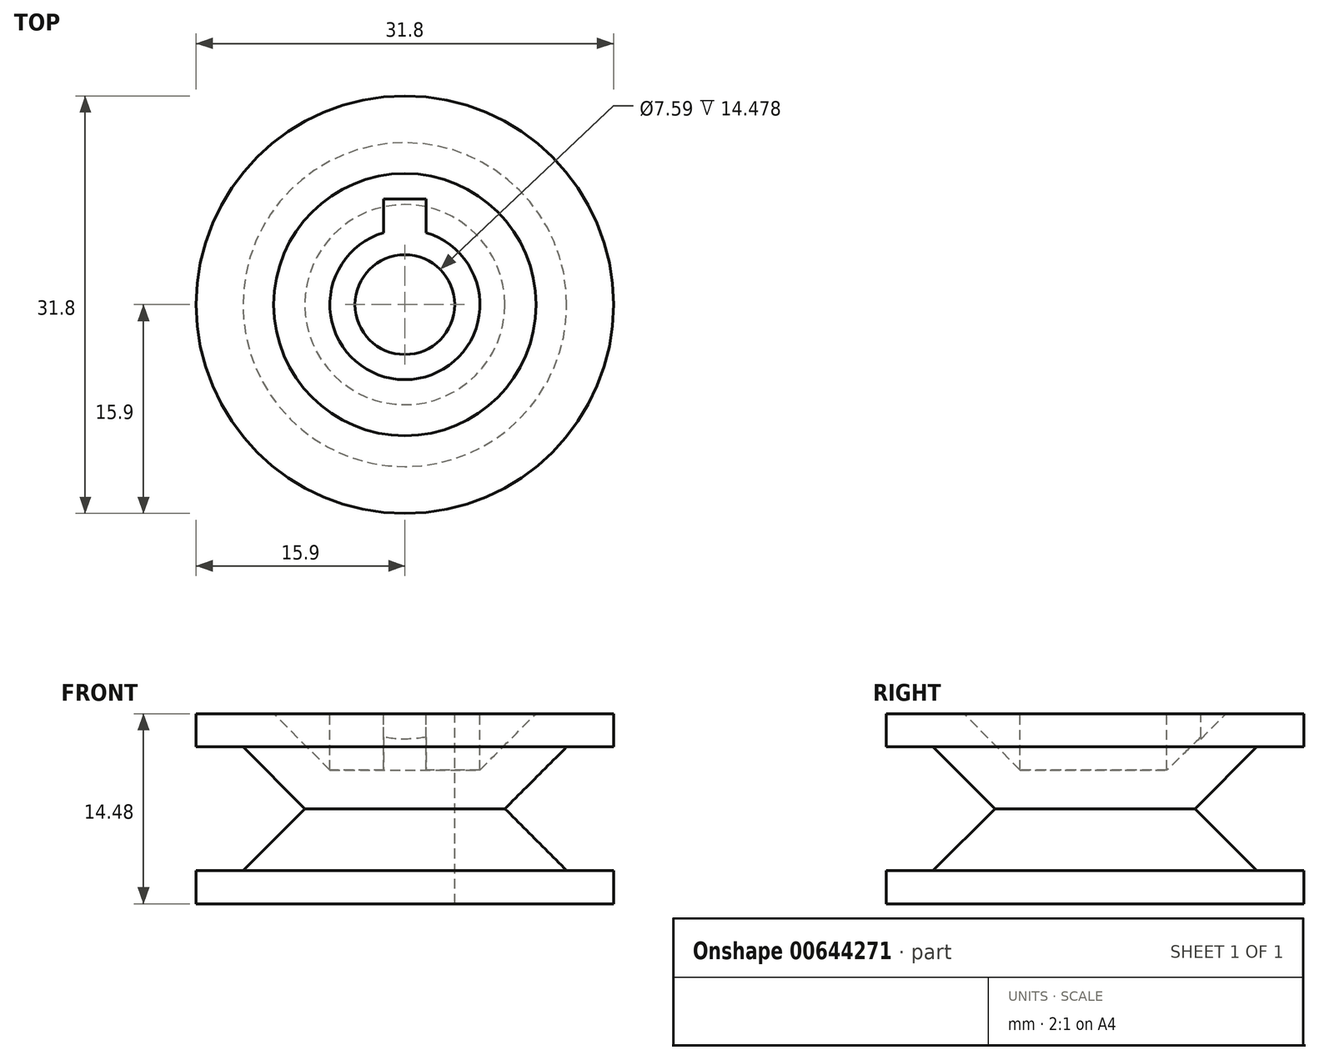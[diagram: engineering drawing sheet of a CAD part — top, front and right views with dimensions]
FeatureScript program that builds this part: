
annotation { "Feature Type Name" : "Feature", "Feature Type Description" : "" }
export const myFeature = defineFeature(function(context is Context, id is Id, definition is map)
    precondition{}
    {
        {
            var Q0;
            Q0=qCreatedBy(makeId("Top.planeOp"),FACE);
            var sketch = newSketch(context, id + "F0", { "sketchPlane" : qUnion([Q0])});
            skCircle(sketch, "E0", {"center": v(0, 0) * mm, "radius": 15.9 * mm});
            skSolve(sketch);
        }
        {
            var Q0;
            Q0 = qSketchRegion(id + "F0", true);
            extrude(context, id + "F1", {"entities" : qUnion([Q0]), "endBound" : BoundingType.SYMMETRIC, "depth" : 14.48 * mm, "offsetDistance" : 25.4 * mm});
        }
        {
            var Q0;
            Q0=makeQuery(id+"F1.opExtrude","CAP_FACE",FACE,{"disambiguationData":[OSD([sQuery(id+"F0.wireOp",EDGE,"E0")])],"isStart":false});
            var sketch = newSketch(context, id + "F2", { "sketchPlane" : qUnion([Q0])});
            skCircle(sketch, "E1", {"center": v(0, 0) * mm, "radius": 3.8 * mm});
            skSolve(sketch);
        }
        {
            var Q0;
            Q0=makeQuery(id+"F2.imprint","IMPRINT",FACE,{"disambiguationData":[TD([[makeQuery(id+"F2.imprint","IMPRINT",EDGE,{"derivedFrom":sQuery(id+"F2.wireOp",EDGE,"E1")}),1.0]])]});
            extrude(context, id + "F3", {"entities" : qUnion([Q0]), "operationType" : NewBodyOperationType.REMOVE, "endBound" : BoundingType.THROUGH_ALL, "oppositeDirection" : true, "depth" : 25.4 * mm, "offsetDistance" : 25.4 * mm});
        }
        {
            var Q0;
            Q0=qCreatedBy(makeId("Right.planeOp"),FACE);
            var sketch = newSketch(context, id + "F4", { "sketchPlane" : qUnion([Q0])});
            skLineSegment(sketch, "E2", {"start": v(21.48, 4.71) * mm, "end": v(12.33, 4.71) * mm});
            skLineSegment(sketch, "E3", {"start": v(12.33, 4.71) * mm, "end": v(7.62, 0) * mm});
            skLineSegment(sketch, "E4", {"start": v(7.62, 0) * mm, "end": v(12.33, -4.71) * mm});
            skLineSegment(sketch, "E5", {"start": v(12.33, -4.71) * mm, "end": v(21.48, -4.71) * mm});
            skLineSegment(sketch, "E6", {"start": v(21.48, -4.71) * mm, "end": v(21.48, 4.71) * mm});
            skLineSegment(sketch, "E7", {"start": v(0, 0) * mm, "end": v(0, 14.85) * mm, "construction": true});
            skLineSegment(sketch, "E8", {"start": v(5.72, 9.28) * mm, "end": v(5.72, 2.94) * mm});
            skLineSegment(sketch, "E9", {"start": v(5.72, 2.94) * mm, "end": v(12.02, 9.28) * mm});
            skLineSegment(sketch, "E10", {"start": v(12.02, 9.28) * mm, "end": v(5.71, 9.28) * mm});
            skSolve(sketch);
        }
        {
            var Q0;
            Q0 = qSketchRegion(id + "F4", true);
            var Q1;
            Q1=sQuery(id+"F4.wireOp",EDGE,"E7");
            revolve(context, id + "F5", {"operationType" : NewBodyOperationType.REMOVE, "entities" : qUnion([Q0]), "axis" : qUnion([Q1]), "revolveType" : RevolveType.FULL, "oppositeDirection" : true});
        }
        {
            var Q0;
            {var subQ0=sQuery(id+"F0.wireOp",EDGE,"E0");Q0=makeQuery(id+"F5.boolean.opBoolean","SPLIT",FACE,{"disambiguationData":[TD([makeQuery(id+"F1.opExtrude","SWEPT_FACE",FACE,{"disambiguationData":[OSD([subQ0])]})])],"derivedFrom":makeQuery(id+"F1.opExtrude","CAP_FACE",FACE,{"disambiguationData":[OSD([subQ0])],"isStart":false})});}
            var sketch = newSketch(context, id + "F6", { "sketchPlane" : qUnion([Q0])});
            skLineSegment(sketch, "E11.bottom", {"start": v(-1.61, 4.88) * mm, "end": v(1.61, 4.88) * mm});
            skLineSegment(sketch, "E11.top", {"start": v(-1.61, 8.06) * mm, "end": v(1.61, 8.06) * mm});
            skLineSegment(sketch, "E11.left", {"start": v(-1.61, 4.88) * mm, "end": v(-1.61, 8.06) * mm});
            skLineSegment(sketch, "E11.right", {"start": v(1.61, 4.88) * mm, "end": v(1.61, 8.06) * mm});
            skPoint(sketch, "E11.middle", {"position": v(0, 6.47) * mm});
            skSolve(sketch);
        }
        {
            var Q0;
            Q0=makeQuery(id+"F6.imprint","IMPRINT",FACE,{"disambiguationData":[TD([[makeQuery(id+"F6.imprint","IMPRINT",EDGE,{"derivedFrom":sQuery(id+"F6.wireOp",EDGE,"E11.bottom")}),1.0]])]});
            var Q1;
            Q1=makeQuery(id+"F5.boolean.opBoolean","COPY",FACE,{"derivedFrom":makeQuery(id+"F5.opRevolve","SWEPT_FACE",FACE,{"disambiguationData":[OSD([sQuery(id+"F4.wireOp",EDGE,"E9")])]})});
            extrude(context, id + "F7", {"entities" : qUnion([Q0]), "operationType" : NewBodyOperationType.ADD, "endBound" : BoundingType.UP_TO_SURFACE, "oppositeDirection" : true, "depth" : 25.4 * mm, "endBoundEntityFace" : qUnion([Q1]), "offsetDistance" : 25.4 * mm});
        }
    });
